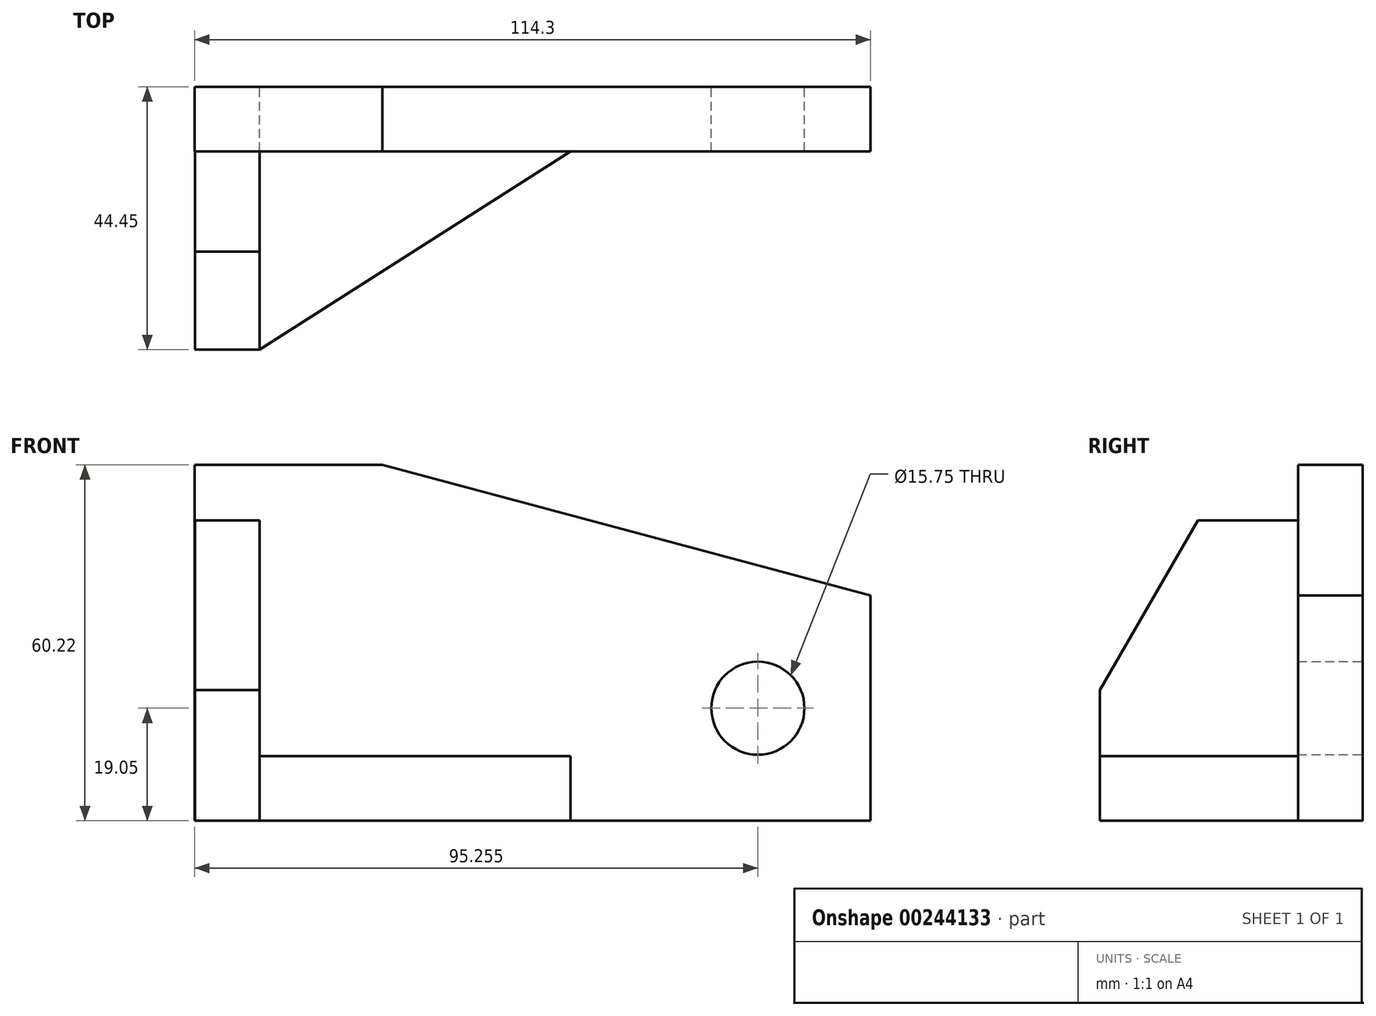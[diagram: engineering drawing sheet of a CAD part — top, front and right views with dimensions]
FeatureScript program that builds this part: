
annotation { "Feature Type Name" : "Feature", "Feature Type Description" : "" }
export const myFeature = defineFeature(function(context is Context, id is Id, definition is map)
    precondition{}
    {
        {
            var Q0;
            Q0=qCreatedBy(makeId("Front.planeOp"),FACE);
            var sketch = newSketch(context, id + "F0", { "sketchPlane" : qUnion([Q0])});
            skLineSegment(sketch, "E0.bottom", {"start": v(-0.09, 60.22) * mm, "end": v(31.66, 60.22) * mm});
            skLineSegment(sketch, "E0.top", {"start": v(-0.09, 0.02) * mm, "end": v(114.21, 0.02) * mm});
            skLineSegment(sketch, "E0.left", {"start": v(-0.09, 60.22) * mm, "end": v(-0.09, 0.02) * mm});
            skLineSegment(sketch, "E0.right", {"start": v(114.21, 38.1) * mm, "end": v(114.21, 0.02) * mm});
            skCircle(sketch, "E1", {"center": v(95.16, 19.05) * mm, "radius": 7.87 * mm});
            skLineSegment(sketch, "E2", {"start": v(31.66, 60.22) * mm, "end": v(114.21, 38.1) * mm});
            skSolve(sketch);
        }
        {
            var Q0;
            Q0=makeQuery(id+"F0.imprint","IMPRINT",FACE,{"disambiguationData":[TD([[makeQuery(id+"F0.imprint","IMPRINT",EDGE,{"derivedFrom":sQuery(id+"F0.wireOp",EDGE,"E0.bottom")}),-1.0]])]});
            extrude(context, id + "F1", {"entities" : qUnion([Q0]), "depth" : 10.92 * mm});
        }
        {
            var Q0;
            Q0=qCreatedBy(makeId("Right.planeOp"),FACE);
            var sketch = newSketch(context, id + "F2", { "sketchPlane" : qUnion([Q0])});
            skLineSegment(sketch, "E3", {"start": v(0, 50.8) * mm, "end": v(0, 0) * mm});
            skLineSegment(sketch, "E4", {"start": v(0, 0) * mm, "end": v(-44.45, 0) * mm});
            skLineSegment(sketch, "E5", {"start": v(0, 50.8) * mm, "end": v(-27.88, 50.8) * mm});
            skLineSegment(sketch, "E6", {"start": v(-44.45, 22.1) * mm, "end": v(-44.45, 0) * mm});
            skLineSegment(sketch, "E7", {"start": v(-44.45, 0) * mm, "end": v(-44.45, 22.1) * mm});
            skLineSegment(sketch, "E8", {"start": v(-44.45, 22.1) * mm, "end": v(-27.88, 50.8) * mm});
            skSolve(sketch);
        }
        {
            var Q0;
            Q0=makeQuery(id+"F2.imprint","IMPRINT",FACE,{"disambiguationData":[TD([[makeQuery(id+"F2.imprint","IMPRINT",EDGE,{"derivedFrom":sQuery(id+"F2.wireOp",EDGE,"E3")}),-1.0]])]});
            extrude(context, id + "F3", {"entities" : qUnion([Q0]), "operationType" : NewBodyOperationType.ADD, "depth" : 10.92 * mm});
        }
        {
            var Q0;
            Q0=qCreatedBy(makeId("Top.planeOp"),FACE);
            var sketch = newSketch(context, id + "F4", { "sketchPlane" : qUnion([Q0])});
            skLineSegment(sketch, "E9", {"start": v(10.92, -44.45) * mm, "end": v(10.92, -10.92) * mm});
            skLineSegment(sketch, "E10", {"start": v(10.92, -10.92) * mm, "end": v(63.5, -10.92) * mm});
            skLineSegment(sketch, "E11", {"start": v(10.92, -44.45) * mm, "end": v(63.5, -10.92) * mm});
            skSolve(sketch);
        }
        {
            var Q0;
            Q0=makeQuery(id+"F4.imprint","IMPRINT",FACE,{"disambiguationData":[TD([[makeQuery(id+"F4.imprint","IMPRINT",EDGE,{"derivedFrom":sQuery(id+"F4.wireOp",EDGE,"E9")}),-1.0]])]});
            extrude(context, id + "F5", {"entities" : qUnion([Q0]), "operationType" : NewBodyOperationType.ADD, "depth" : 10.92 * mm});
        }
    });
